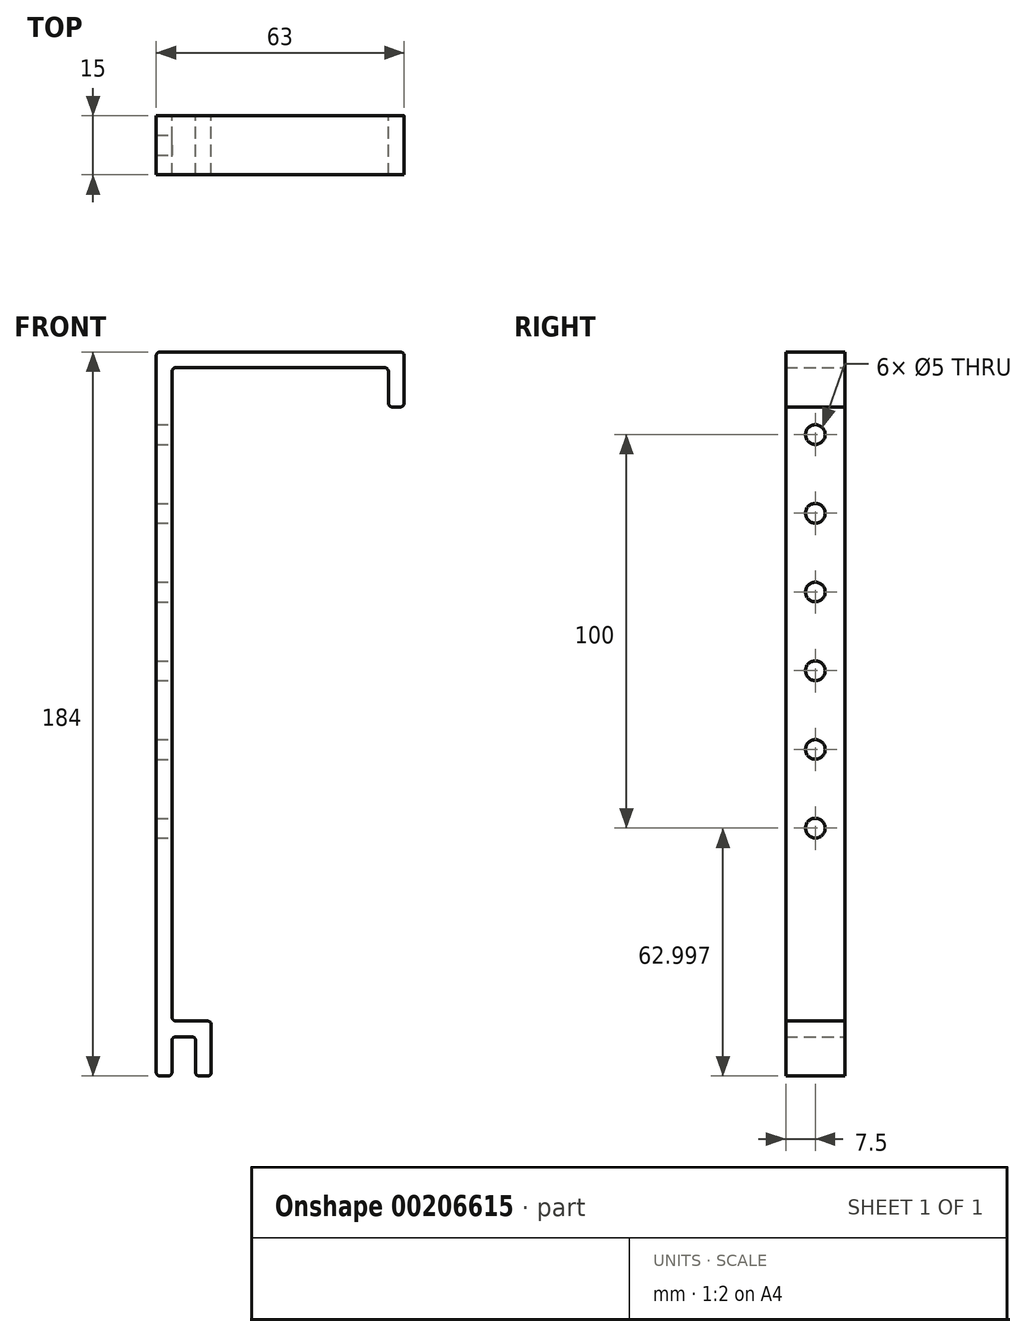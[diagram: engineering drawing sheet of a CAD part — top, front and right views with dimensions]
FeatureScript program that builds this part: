
annotation { "Feature Type Name" : "Feature", "Feature Type Description" : "" }
export const myFeature = defineFeature(function(context is Context, id is Id, definition is map)
    precondition{}
    {
        {
            var Q0;
            Q0=qCreatedBy(makeId("Front.planeOp"),FACE);
            var sketch = newSketch(context, id + "F0", { "sketchPlane" : qUnion([Q0])});
            skLineSegment(sketch, "E0", {"start": v(-22.55, -101.14) * mm, "end": v(-22.55, 62.86) * mm});
            skLineSegment(sketch, "E1", {"start": v(-21.55, 63.86) * mm, "end": v(31.45, 63.86) * mm});
            skLineSegment(sketch, "E2", {"start": v(32.45, 62.86) * mm, "end": v(32.45, 54.86) * mm});
            skLineSegment(sketch, "E3", {"start": v(33.45, 53.86) * mm, "end": v(35.45, 53.86) * mm});
            skLineSegment(sketch, "E4", {"start": v(36.45, 54.86) * mm, "end": v(36.45, 66.86) * mm});
            skLineSegment(sketch, "E5", {"start": v(35.45, 67.86) * mm, "end": v(-25.55, 67.86) * mm});
            skLineSegment(sketch, "E6", {"start": v(-26.55, 66.86) * mm, "end": v(-26.55, -106.14) * mm});
            skLineSegment(sketch, "E7", {"start": v(-26.55, -106.14) * mm, "end": v(-26.55, -115.14) * mm});
            skLineSegment(sketch, "E8", {"start": v(-25.55, -116.14) * mm, "end": v(-23.55, -116.14) * mm});
            skLineSegment(sketch, "E9", {"start": v(-22.55, -115.14) * mm, "end": v(-22.55, -107.14) * mm});
            skLineSegment(sketch, "E10", {"start": v(-21.55, -106.14) * mm, "end": v(-17.55, -106.14) * mm});
            skLineSegment(sketch, "E11", {"start": v(-16.55, -107.14) * mm, "end": v(-16.55, -115.14) * mm});
            skLineSegment(sketch, "E12", {"start": v(-15.55, -116.14) * mm, "end": v(-13.55, -116.14) * mm});
            skLineSegment(sketch, "E13", {"start": v(-12.55, -115.14) * mm, "end": v(-12.55, -103.14) * mm});
            skLineSegment(sketch, "E14", {"start": v(-13.55, -102.14) * mm, "end": v(-21.55, -102.14) * mm});
            skPoint(sketch, "E15.visualSharp", {"position": v(-26.55, 67.86) * mm});
            skArc(sketch, "E15.filletArc", {"start": v(-25.55, 67.86) * mm, "mid": v(-26.26, 67.56) * mm, "end": v(-26.55, 66.86) * mm});
            skPoint(sketch, "E16.visualSharp", {"position": v(-22.55, 63.86) * mm});
            skArc(sketch, "E16.filletArc", {"start": v(-21.55, 63.86) * mm, "mid": v(-22.26, 63.56) * mm, "end": v(-22.55, 62.86) * mm});
            skPoint(sketch, "E17.visualSharp", {"position": v(32.45, 63.86) * mm});
            skArc(sketch, "E17.filletArc", {"start": v(32.45, 62.86) * mm, "mid": v(32.16, 63.56) * mm, "end": v(31.45, 63.86) * mm});
            skPoint(sketch, "E18.visualSharp", {"position": v(36.45, 67.86) * mm});
            skArc(sketch, "E18.filletArc", {"start": v(36.45, 66.86) * mm, "mid": v(36.16, 67.56) * mm, "end": v(35.45, 67.86) * mm});
            skPoint(sketch, "E19.visualSharp", {"position": v(36.45, 53.86) * mm});
            skArc(sketch, "E19.filletArc", {"start": v(35.45, 53.86) * mm, "mid": v(36.16, 54.15) * mm, "end": v(36.45, 54.86) * mm});
            skPoint(sketch, "E20.visualSharp", {"position": v(32.45, 53.86) * mm});
            skArc(sketch, "E20.filletArc", {"start": v(32.45, 54.86) * mm, "mid": v(32.74, 54.15) * mm, "end": v(33.45, 53.86) * mm});
            skPoint(sketch, "E21.visualSharp", {"position": v(-22.55, -102.14) * mm});
            skArc(sketch, "E21.filletArc", {"start": v(-22.55, -101.14) * mm, "mid": v(-22.26, -101.85) * mm, "end": v(-21.55, -102.14) * mm});
            skPoint(sketch, "E22.visualSharp", {"position": v(-12.55, -102.14) * mm});
            skArc(sketch, "E22.filletArc", {"start": v(-12.55, -103.14) * mm, "mid": v(-12.84, -102.44) * mm, "end": v(-13.55, -102.14) * mm});
            skPoint(sketch, "E23.visualSharp", {"position": v(-16.55, -106.14) * mm});
            skArc(sketch, "E23.filletArc", {"start": v(-16.55, -107.14) * mm, "mid": v(-16.84, -106.44) * mm, "end": v(-17.55, -106.14) * mm});
            skPoint(sketch, "E24.visualSharp", {"position": v(-22.55, -106.14) * mm});
            skArc(sketch, "E24.filletArc", {"start": v(-21.55, -106.14) * mm, "mid": v(-22.26, -106.44) * mm, "end": v(-22.55, -107.14) * mm});
            skPoint(sketch, "E25.visualSharp", {"position": v(-16.55, -116.14) * mm});
            skArc(sketch, "E25.filletArc", {"start": v(-16.55, -115.14) * mm, "mid": v(-16.26, -115.85) * mm, "end": v(-15.55, -116.14) * mm});
            skPoint(sketch, "E26.visualSharp", {"position": v(-12.55, -116.14) * mm});
            skArc(sketch, "E26.filletArc", {"start": v(-13.55, -116.14) * mm, "mid": v(-12.84, -115.85) * mm, "end": v(-12.55, -115.14) * mm});
            skPoint(sketch, "E27.visualSharp", {"position": v(-22.55, -116.14) * mm});
            skArc(sketch, "E27.filletArc", {"start": v(-23.55, -116.14) * mm, "mid": v(-22.84, -115.85) * mm, "end": v(-22.55, -115.14) * mm});
            skPoint(sketch, "E28.visualSharp", {"position": v(-26.55, -116.14) * mm});
            skArc(sketch, "E28.filletArc", {"start": v(-26.55, -115.14) * mm, "mid": v(-26.26, -115.85) * mm, "end": v(-25.55, -116.14) * mm});
            skSolve(sketch);
        }
        {
            var Q0;
            Q0=makeQuery(id+"F0.imprint","IMPRINT",FACE,{"disambiguationData":[TD([[makeQuery(id+"F0.imprint","IMPRINT",EDGE,{"derivedFrom":sQuery(id+"F0.wireOp",EDGE,"E0")}),1.0]])]});
            extrude(context, id + "F1", {"entities" : qUnion([Q0]), "depth" : 15 * mm});
        }
        {
            var Q0;
            Q0=qCreatedBy(makeId("Right.planeOp"),FACE);
            var sketch = newSketch(context, id + "F2", { "sketchPlane" : qUnion([Q0])});
            skCircle(sketch, "E29", {"center": v(-7.5, 46.86) * mm, "radius": 3 * mm});
            skCircle(sketch, "E30.1.0.0", {"center": v(-7.5, 26.86) * mm, "radius": 3 * mm});
            skCircle(sketch, "E30.2.0.0", {"center": v(-7.5, 6.86) * mm, "radius": 3 * mm});
            skCircle(sketch, "E30.3.0.0", {"center": v(-7.5, -13.14) * mm, "radius": 3 * mm});
            skCircle(sketch, "E30.4.0.0", {"center": v(-7.5, -33.14) * mm, "radius": 3 * mm});
            skCircle(sketch, "E30.5.0.0", {"center": v(-7.5, -53.14) * mm, "radius": 3 * mm});
            skLineSegment(sketch, "E30.direction1", {"start": v(-7.5, 46.86) * mm, "end": v(-7.5, 26.86) * mm, "construction": true});
            skSolve(sketch);
        }
        {
            var Q0;
            Q0=sQuery(id+"F2.wireOp",VERTEX,"E30.direction1.end");
            var Q1;
            Q1=sQuery(id+"F2.wireOp",VERTEX,"E30.direction1.start");
            var Q2;
            Q2=sQuery(id+"F2.wireOp",VERTEX,"E30.2.0.0.center");
            var Q3;
            Q3=sQuery(id+"F2.wireOp",VERTEX,"E30.3.0.0.center");
            var Q4;
            Q4=sQuery(id+"F2.wireOp",VERTEX,"E30.4.0.0.center");
            var Q5;
            Q5=sQuery(id+"F2.wireOp",VERTEX,"E30.5.0.0.center");
            var Q6;
            Q6=makeQuery(id+"F1.opExtrude","SWEPT_BODY",BODY,{"disambiguationData":[OSD([sQuery(id+"F0.wireOp",EDGE,"E0"),sQuery(id+"F0.wireOp",EDGE,"E1"),sQuery(id+"F0.wireOp",EDGE,"E2"),sQuery(id+"F0.wireOp",EDGE,"E3"),sQuery(id+"F0.wireOp",EDGE,"E4"),sQuery(id+"F0.wireOp",EDGE,"E5"),sQuery(id+"F0.wireOp",EDGE,"E6"),sQuery(id+"F0.wireOp",EDGE,"E7"),sQuery(id+"F0.wireOp",EDGE,"E8"),sQuery(id+"F0.wireOp",EDGE,"E9"),sQuery(id+"F0.wireOp",EDGE,"E10"),sQuery(id+"F0.wireOp",EDGE,"E11"),sQuery(id+"F0.wireOp",EDGE,"E12"),sQuery(id+"F0.wireOp",EDGE,"E13"),sQuery(id+"F0.wireOp",EDGE,"E14"),sQuery(id+"F0.wireOp",EDGE,"E15.filletArc"),sQuery(id+"F0.wireOp",EDGE,"E16.filletArc"),sQuery(id+"F0.wireOp",EDGE,"E17.filletArc"),sQuery(id+"F0.wireOp",EDGE,"E18.filletArc"),sQuery(id+"F0.wireOp",EDGE,"E19.filletArc"),sQuery(id+"F0.wireOp",EDGE,"E20.filletArc"),sQuery(id+"F0.wireOp",EDGE,"E21.filletArc"),sQuery(id+"F0.wireOp",EDGE,"E22.filletArc"),sQuery(id+"F0.wireOp",EDGE,"E23.filletArc"),sQuery(id+"F0.wireOp",EDGE,"E24.filletArc"),sQuery(id+"F0.wireOp",EDGE,"E25.filletArc"),sQuery(id+"F0.wireOp",EDGE,"E26.filletArc"),sQuery(id+"F0.wireOp",EDGE,"E27.filletArc"),sQuery(id+"F0.wireOp",EDGE,"E28.filletArc")])]});
            hole(context, id + "F3", {"style" : HoleStyle.SIMPLE, "endStyle" : HoleEndStyle.THROUGH, "holeDiameter" : 5 * mm, "locations" : qUnion([Q0, Q1, Q2, Q3, Q4, Q5]), "scope" : qUnion([Q6]), "isTappedThrough" : true});
        }
    });
